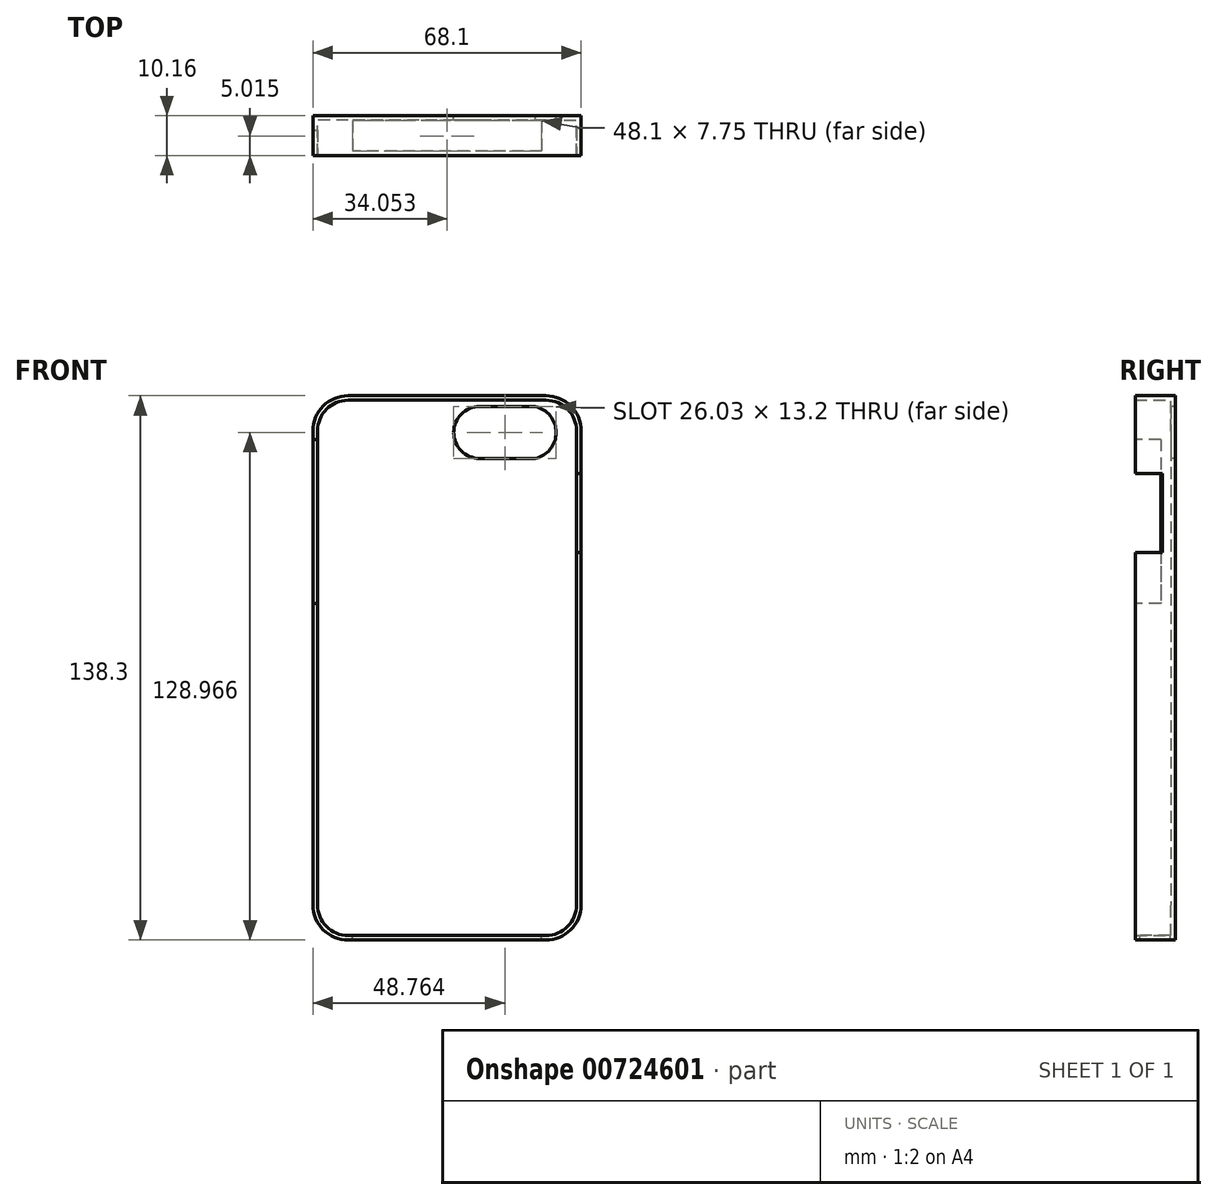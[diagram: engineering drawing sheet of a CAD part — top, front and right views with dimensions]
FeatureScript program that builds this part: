
annotation { "Feature Type Name" : "Feature", "Feature Type Description" : "" }
export const myFeature = defineFeature(function(context is Context, id is Id, definition is map)
    precondition{}
    {
        {
            var Q0;
            Q0=qCreatedBy(makeId("Front.planeOp"),FACE);
            var sketch = newSketch(context, id + "F0", { "sketchPlane" : qUnion([Q0])});
            skLineSegment(sketch, "E0.bottom", {"start": v(34.05, 69.15) * mm, "end": v(-34.05, 69.15) * mm});
            skLineSegment(sketch, "E0.top", {"start": v(34.05, -69.15) * mm, "end": v(-34.05, -69.15) * mm});
            skLineSegment(sketch, "E0.left", {"start": v(34.05, 69.15) * mm, "end": v(34.05, -69.15) * mm});
            skLineSegment(sketch, "E0.right", {"start": v(-34.05, 69.15) * mm, "end": v(-34.05, -69.15) * mm});
            skPoint(sketch, "E0.middle", {"position": v(0, 0) * mm});
            skSolve(sketch);
        }
        {
            var Q0;
            Q0=makeQuery(id+"F0.imprint","IMPRINT",FACE,{"disambiguationData":[TD([[makeQuery(id+"F0.imprint","IMPRINT",EDGE,{"derivedFrom":sQuery(id+"F0.wireOp",EDGE,"E0.bottom")}),1.0]])]});
            extrude(context, id + "F1", {"entities" : qUnion([Q0]), "endBound" : BoundingType.SYMMETRIC, "depth" : 10.16 * mm});
        }
        {
            var Q0;
            Q0=makeQuery(id+"F1.opExtrude","SWEPT_EDGE",EDGE,{"disambiguationData":[OSD([sQuery(id+"F0.wireOp",EDGE,"E0.bottom"),sQuery(id+"F0.wireOp",EDGE,"E0.right")])]});
            var Q1;
            Q1=makeQuery(id+"F1.opExtrude","SWEPT_EDGE",EDGE,{"disambiguationData":[OSD([sQuery(id+"F0.wireOp",EDGE,"E0.bottom"),sQuery(id+"F0.wireOp",EDGE,"E0.left")])]});
            var Q2;
            Q2=makeQuery(id+"F1.opExtrude","SWEPT_EDGE",EDGE,{"disambiguationData":[OSD([sQuery(id+"F0.wireOp",EDGE,"E0.top"),sQuery(id+"F0.wireOp",EDGE,"E0.left")])]});
            var Q3;
            Q3=makeQuery(id+"F1.opExtrude","SWEPT_EDGE",EDGE,{"disambiguationData":[OSD([sQuery(id+"F0.wireOp",EDGE,"E0.top"),sQuery(id+"F0.wireOp",EDGE,"E0.right")])]});
            fillet(context, id + "F2", {"entities" : qUnion([Q0, Q1, Q2, Q3]), "radius" : 8.93 * mm, "tangentPropagation" : true, "allowEdgeOverflow" : false});
        }
        {
            var Q0;
            Q0=makeQuery(id+"F1.opExtrude","CAP_FACE",FACE,{"disambiguationData":[OSD([sQuery(id+"F0.wireOp",EDGE,"E0.bottom"),sQuery(id+"F0.wireOp",EDGE,"E0.top"),sQuery(id+"F0.wireOp",EDGE,"E0.left"),sQuery(id+"F0.wireOp",EDGE,"E0.right")])],"isStart":false});
            shell(context, id + "F3", {"entities" : qUnion([Q0]), "thickness" : 1.15 * mm});
        }
        {
            var Q0;
            Q0=makeQuery(id+"F0.imprint","IMPRINT",FACE,{"disambiguationData":[TD([[makeQuery(id+"F0.imprint","IMPRINT",EDGE,{"derivedFrom":sQuery(id+"F0.wireOp",EDGE,"E0.bottom")}),1.0]])]});
            var sketch = newSketch(context, id + "F4", { "sketchPlane" : qUnion([Q0])});
            skLineSegment(sketch, "E1.bottom", {"start": v(27.4, 66.41) * mm, "end": v(3.3, 66.41) * mm});
            skLineSegment(sketch, "E1.top", {"start": v(27.4, 53.22) * mm, "end": v(3.3, 53.22) * mm});
            skLineSegment(sketch, "E1.left", {"start": v(27.4, 66.41) * mm, "end": v(27.4, 53.22) * mm});
            skLineSegment(sketch, "E1.right", {"start": v(3.3, 66.41) * mm, "end": v(3.3, 53.22) * mm});
            skSolve(sketch);
        }
        {
            var Q0;
            Q0=qSketchRegion(id+"F4",true);
            extrude(context, id + "F5", {"entities" : qUnion([Q0]), "operationType" : NewBodyOperationType.REMOVE, "endBound" : BoundingType.SYMMETRIC, "depth" : 25 * mm});
        }
        {
            var Q0;
            Q0=makeQuery(id+"F1.opExtrude","SWEPT_FACE",FACE,{"disambiguationData":[OSD([sQuery(id+"F0.wireOp",EDGE,"E0.top")])]});
            var sketch = newSketch(context, id + "F6", { "sketchPlane" : qUnion([Q0])});
            skLineSegment(sketch, "E2.bottom", {"start": v(-24.05, 3.94) * mm, "end": v(24.05, 3.94) * mm});
            skLineSegment(sketch, "E2.top", {"start": v(-24.05, -3.81) * mm, "end": v(24.05, -3.81) * mm});
            skLineSegment(sketch, "E2.left", {"start": v(-24.05, 3.94) * mm, "end": v(-24.05, -3.81) * mm});
            skLineSegment(sketch, "E2.right", {"start": v(24.05, 3.94) * mm, "end": v(24.05, -3.81) * mm});
            skSolve(sketch);
        }
        {
            var Q0;
            {var subQ0=sQuery(id+"F6.wireOp",EDGE,"E2.bottom");Q0=makeQuery(id+"F6.imprint","IMPRINT",FACE,{"disambiguationData":[TD([[makeQuery(id+"F6.imprint","IMPRINT",EDGE,{"derivedFrom":subQ0}),-1.0]])]});}
            var Q1;
            {var subQ0=sQuery(id+"F6.wireOp",EDGE,"E2.top");Q1=makeQuery(id+"F6.imprint","IMPRINT",FACE,{"disambiguationData":[TD([[makeQuery(id+"F6.imprint","IMPRINT",EDGE,{"derivedFrom":subQ0}),1.0]])]});}
            extrude(context, id + "F7", {"entities" : qUnion([Q0, Q1]), "operationType" : NewBodyOperationType.REMOVE, "endBound" : BoundingType.SYMMETRIC, "depth" : 25 * mm});
        }
        {
            var Q0;
            Q0=makeQuery(id+"F1.opExtrude","SWEPT_FACE",FACE,{"disambiguationData":[OSD([sQuery(id+"F0.wireOp",EDGE,"E0.right")])]});
            var sketch = newSketch(context, id + "F8", { "sketchPlane" : qUnion([Q0])});
            skLineSegment(sketch, "E3.bottom", {"start": v(-1.38, 58.06) * mm, "end": v(8.73, 58.06) * mm});
            skLineSegment(sketch, "E3.top", {"start": v(-1.38, 16.4) * mm, "end": v(8.73, 16.4) * mm});
            skLineSegment(sketch, "E3.left", {"start": v(-1.38, 58.06) * mm, "end": v(-1.38, 16.4) * mm});
            skLineSegment(sketch, "E3.right", {"start": v(8.73, 58.06) * mm, "end": v(8.73, 16.4) * mm});
            skSolve(sketch);
        }
        {
            var Q0;
            Q0=qSketchRegion(id+"F8",true);
            extrude(context, id + "F9", {"entities" : qUnion([Q0]), "operationType" : NewBodyOperationType.REMOVE, "endBound" : BoundingType.SYMMETRIC, "depth" : 25 * mm});
        }
        {
            var Q0;
            Q0=makeQuery(id+"F1.opExtrude","SWEPT_FACE",FACE,{"disambiguationData":[OSD([sQuery(id+"F0.wireOp",EDGE,"E0.left")])]});
            var sketch = newSketch(context, id + "F10", { "sketchPlane" : qUnion([Q0])});
            skLineSegment(sketch, "E4.bottom", {"start": v(-5.08, 49.35) * mm, "end": v(1.78, 49.35) * mm});
            skLineSegment(sketch, "E4.top", {"start": v(-5.08, 29.37) * mm, "end": v(1.78, 29.37) * mm});
            skLineSegment(sketch, "E4.left", {"start": v(-5.08, 49.35) * mm, "end": v(-5.08, 29.37) * mm});
            skLineSegment(sketch, "E4.right", {"start": v(1.78, 49.35) * mm, "end": v(1.78, 29.37) * mm});
            skSolve(sketch);
        }
        {
            var Q0;
            Q0=makeQuery(id+"F10.imprint","IMPRINT",FACE,{"disambiguationData":[TD([[makeQuery(id+"F10.imprint","IMPRINT",EDGE,{"derivedFrom":sQuery(id+"F10.wireOp",EDGE,"E4.bottom")}),-1.0]])]});
            extrude(context, id + "F11", {"entities" : qUnion([Q0]), "operationType" : NewBodyOperationType.REMOVE, "endBound" : BoundingType.SYMMETRIC, "depth" : 25 * mm});
        }
        {
            var Q0;
            Q0=makeQuery(id+"F5.boolean.opBoolean","COPY",EDGE,{"derivedFrom":makeQuery(id+"F5.opExtrude","SWEPT_EDGE",EDGE,{"disambiguationData":[OSD([sQuery(id+"F4.wireOp",EDGE,"E1.bottom"),sQuery(id+"F4.wireOp",EDGE,"E1.right")])]})});
            var Q1;
            Q1=makeQuery(id+"F5.boolean.opBoolean","COPY",EDGE,{"derivedFrom":makeQuery(id+"F5.opExtrude","SWEPT_EDGE",EDGE,{"disambiguationData":[OSD([sQuery(id+"F4.wireOp",EDGE,"E1.bottom"),sQuery(id+"F4.wireOp",EDGE,"E1.left")])]})});
            var Q2;
            Q2=makeQuery(id+"F5.boolean.opBoolean","COPY",EDGE,{"derivedFrom":makeQuery(id+"F5.opExtrude","SWEPT_EDGE",EDGE,{"disambiguationData":[OSD([sQuery(id+"F4.wireOp",EDGE,"E1.top"),sQuery(id+"F4.wireOp",EDGE,"E1.left")])]})});
            var Q3;
            Q3=makeQuery(id+"F5.boolean.opBoolean","COPY",EDGE,{"derivedFrom":makeQuery(id+"F5.opExtrude","SWEPT_EDGE",EDGE,{"disambiguationData":[OSD([sQuery(id+"F4.wireOp",EDGE,"E1.top"),sQuery(id+"F4.wireOp",EDGE,"E1.right")])]})});
            chamfer(context, id + "F12", {"entities" : qUnion([Q0, Q1, Q2, Q3]), "width" : 5 * mm, "tangentPropagation" : true});
        }
        {
            var Q0;
            Q0=makeQuery(id+"F1.opExtrude","CAP_FACE",FACE,{"disambiguationData":[OSD([sQuery(id+"F0.wireOp",EDGE,"E0.bottom"),sQuery(id+"F0.wireOp",EDGE,"E0.top"),sQuery(id+"F0.wireOp",EDGE,"E0.left"),sQuery(id+"F0.wireOp",EDGE,"E0.right")])],"isStart":true});
            var sketch = newSketch(context, id + "F13", { "sketchPlane" : qUnion([Q0])});
            skArc(sketch, "E5", {"start": v(-22.4, 66.41) * mm, "mid": v(-27.73, 59.82) * mm, "end": v(-22.4, 53.22) * mm});
            skArc(sketch, "E6", {"start": v(-8.3, 53.22) * mm, "mid": v(-3.22, 59.82) * mm, "end": v(-8.3, 66.41) * mm});
            skSolve(sketch);
        }
        {
            var Q0;
            Q0=qSketchRegion(id+"F13",true);
            var Q1;
            Q1=makeQuery(id+"F13.imprint","IMPRINT",FACE,{"disambiguationData":[TD([[makeQuery(id+"F13.imprint","IMPRINT",EDGE,{"derivedFrom":sQuery(id+"F13.wireOp",EDGE,"E5")}),1.0]])]});
            extrude(context, id + "F14", {"entities" : qUnion([Q0, Q1]), "operationType" : NewBodyOperationType.REMOVE, "oppositeDirection" : true, "depth" : 25 * mm, "offsetDistance" : 25 * mm});
        }
        {
            var Q0;
            Q0=makeQuery(id+"F1.opExtrude","CAP_FACE",FACE,{"disambiguationData":[OSD([sQuery(id+"F0.wireOp",EDGE,"E0.bottom"),sQuery(id+"F0.wireOp",EDGE,"E0.top"),sQuery(id+"F0.wireOp",EDGE,"E0.left"),sQuery(id+"F0.wireOp",EDGE,"E0.right")])],"isStart":true});
            var sketch = newSketch(context, id + "F15", { "sketchPlane" : qUnion([Q0])});
            skArc(sketch, "E7", {"start": v(-8.3, 53.22) * mm, "mid": v(-1.7, 59.82) * mm, "end": v(-8.3, 66.41) * mm});
            skSolve(sketch);
        }
        {
            var Q0;
            Q0=qSketchRegion(id+"F15",true);
            var Q1;
            Q1=makeQuery(id+"F15.imprint","IMPRINT",FACE,{"disambiguationData":[TD([[makeQuery(id+"F15.imprint","IMPRINT",EDGE,{"derivedFrom":sQuery(id+"F15.wireOp",EDGE,"E7")}),1.0]])]});
            extrude(context, id + "F16", {"entities" : qUnion([Q0, Q1]), "operationType" : NewBodyOperationType.REMOVE, "oppositeDirection" : true, "depth" : 25 * mm, "offsetDistance" : 25 * mm});
        }
    });
